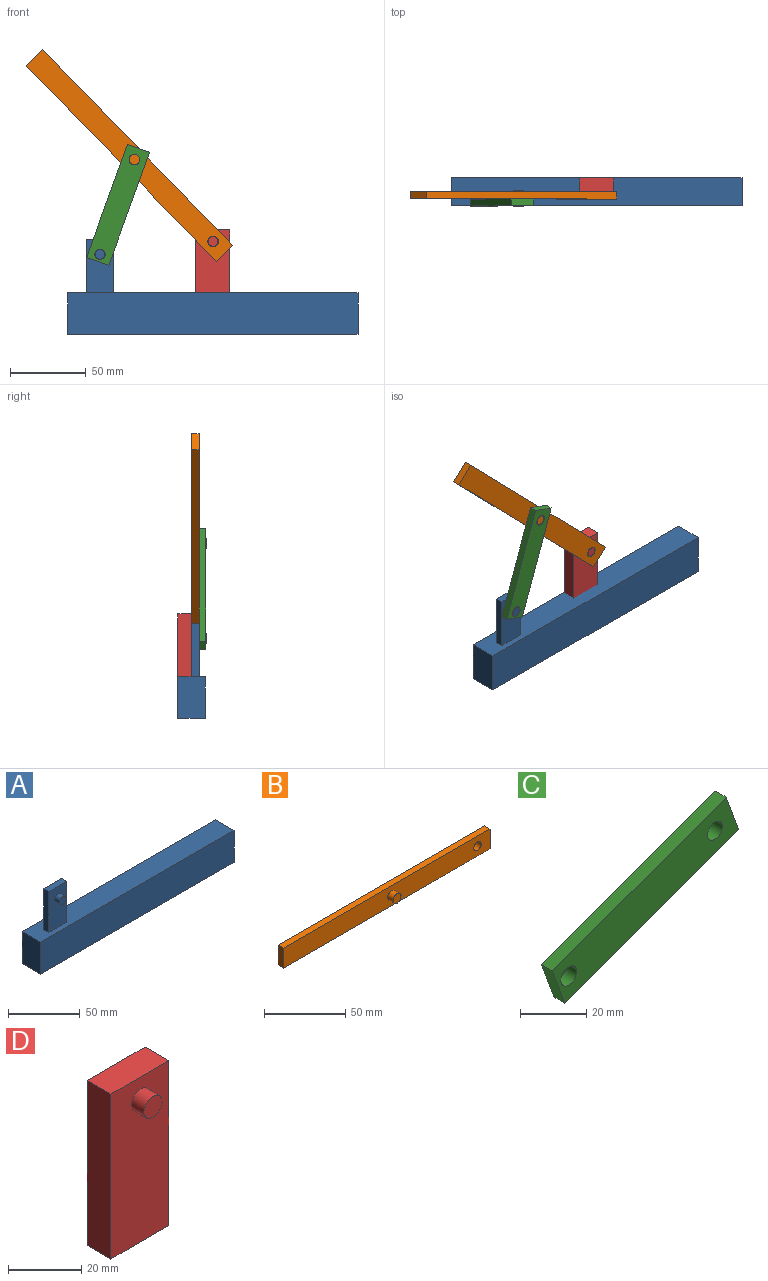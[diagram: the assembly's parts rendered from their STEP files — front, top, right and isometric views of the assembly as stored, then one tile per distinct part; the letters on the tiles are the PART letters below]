
ASSEMBLY  parts=4 mates=4
PART A: 15 faces, bbox 191.4x19x62.4 mm
  f0: cylinder r=3.17mm len=6.35mm, axis (0,-1,0), area 0.4mm2, adj f7,f12
  f1: plane 191.35x18.29mm, normal (0,0,-1), area 3499.5mm2, adj f2,f4,f5,f6
  f2: plane 27.39x18.29mm, normal (1,0,0), area 501mm2, adj f1,f3,f5,f6
  f3: plane 191.35x18.29mm, normal (0,0,1), area 3412.3mm2, adj f2,f4,f5,f6,f7,f8,f9,f10
  f4: plane 27.39x18.29mm, normal (-1,0,0), area 501mm2, adj f1,f3,f5,f6
  f5: plane 191.35x27.39mm, normal (0,-1,0), area 5241.7mm2, adj f1,f2,f3,f4
  f6: plane 191.35x27.39mm, normal (0,1,0), area 5241.7mm2, adj f1,f2,f3,f4
  f7: plane 35.05x17.61mm, normal (0,1,0), area 585.5mm2, adj f0,f3,f8,f10,f11
  f8: plane 35.05x4.95mm, normal (-1,0,0), area 173.5mm2, adj f3,f7,f9,f11
  f9: plane 35.05x17.61mm, normal (0,-1,0), area 584.6mm2, adj f3,f8,f10,f11,f13
  f10: plane 35.05x4.95mm, normal (1,0,0), area 173.5mm2, adj f3,f7,f9,f11
  f11: plane 17.61x4.95mm, normal (0,0,1), area 87.1mm2, adj f7,f8,f9,f10
  f12: plane 6.35x6.35mm, normal (0,1,0), area 31.7mm2, adj f0
  f13: cylinder r=3.22mm len=6.44mm, axis (0,1,0), area 99.7mm2, adj f9,f14
  f14: plane 6.44x6.44mm, normal (0,-1,0), area 32.6mm2, adj f13
PART B: 11 faces, bbox 180x9.9x15.1 mm
  f0: plane 179.95x4.83mm, normal (0,0,1), area 868.4mm2, adj f1,f3,f4,f5
  f1: plane 15.07x4.83mm, normal (-1,0,0), area 72.7mm2, adj f0,f2,f4,f5
  f2: plane 179.95x4.83mm, normal (0,0,-1), area 868.4mm2, adj f1,f3,f4,f5
  f3: plane 15.07x4.83mm, normal (1,0,0), area 72.7mm2, adj f0,f2,f4,f5
  f4: plane 179.95x15.07mm, normal (0,-1,0), area 2641.9mm2, adj f0,f1,f2,f3,f8,f10
  f5: plane 179.95x15.07mm, normal (0,1,0), area 2641.9mm2, adj f0,f1,f2,f3,f7,f10
  f6: plane 6.95x6.95mm, normal (0,1,0), area 37.9mm2, adj f7
  f7: cylinder r=3.47mm len=6.95mm, axis (0,-1,0), area 8.4mm2, adj f5,f6
  f8: cylinder r=3.47mm len=6.95mm, axis (0,-1,0), area 102.4mm2, adj f4,f9
  f9: plane 6.95x6.95mm, normal (0,-1,0), area 37.9mm2, adj f8
  f10: cylinder r=3.17mm len=6.35mm, axis (0,-1,0), area 96.3mm2, adj f4,f5
PART C: 8 faces, bbox 79.6x4.6x41.6 mm
  f0: plane 74.34x27.06mm, normal (-0.34,0,0.94), area 361.7mm2, adj f1,f3,f5,f6
  f1: plane 14.54x5.29mm, normal (-0.94,0,-0.34), area 70.7mm2, adj f0,f2,f5,f6
  f2: plane 74.34x27.06mm, normal (0.34,0,-0.94), area 361.7mm2, adj f1,f3,f5,f6
  f3: plane 14.54x5.29mm, normal (0.94,0,0.34), area 70.7mm2, adj f0,f2,f5,f6
  f4: cylinder r=3.4mm len=6.8mm, axis (0,1,0), area 97.7mm2, adj f5,f6
  f5: plane 79.63x41.59mm, normal (0,-1,0), area 1155.6mm2, adj f0,f1,f2,f3,f4,f7
  f6: plane 79.63x41.59mm, normal (0,1,0), area 1155.6mm2, adj f0,f1,f2,f3,f4,f7
  f7: cylinder r=3.17mm len=6.35mm, axis (0,-1,0), area 91.2mm2, adj f5,f6
PART D: 10 faces, bbox 22.4x14.2x55.1 mm
  f0: plane 22.39x9.14mm, normal (0,0,-1), area 204.6mm2, adj f1,f3,f4,f9
  f1: plane 55.12x9.14mm, normal (-1,0,0), area 503.8mm2, adj f0,f2,f4,f9
  f2: plane 22.39x9.14mm, normal (0,0,1), area 204.6mm2, adj f1,f3,f4,f9
  f3: plane 55.12x9.14mm, normal (1,0,0), area 503.8mm2, adj f0,f2,f4,f9
  f4: plane 55.12x22.39mm, normal (0,1,0), area 1195.4mm2, adj f0,f1,f2,f3,f6
  f5: plane 7x7mm, normal (0,1,0), area 38.4mm2, adj f6
  f6: cylinder r=3.5mm len=7mm, axis (0,-1,0), area 5.7mm2, adj f4,f5
  f7: cylinder r=3.5mm len=7mm, axis (0,-1,0), area 106.1mm2, adj f8,f9
  f8: plane 7x7mm, normal (0,-1,0), area 38.4mm2, adj f7
  f9: plane 55.12x22.39mm, normal (0,-1,0), area 1195.4mm2, adj f0,f1,f2,f3,f7
PLACE A t=(-2.3,-20.28,-2.57)mm fixed
PLACE B rot(axis=(0,1,0),45.8deg) t=(-89.82,-20.41,47.35)mm
PLACE C rot(axis=(0,-1,0),50.2deg) t=(1.03,-20.28,68.53)mm
PLACE D t=(-64.93,-20.41,-16.26)mm
MATE revolute C.f4 <-> A.f0  axis (0,1,0) through (-76.58,-25.23,36.53)mm
MATE revolute B.f10 <-> D.f6  axis (0,1,0) through (-2.04,-20.41,45.02)mm
MATE slider D.f4 <-> A.f6  axis (0,1,0) through (-2.3,-11.27,-2.57)mm
MATE revolute C.f7 <-> B.f7  axis (0,1,0) through (-53.94,-25.23,98.88)mm
